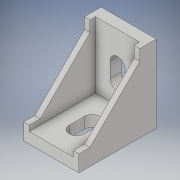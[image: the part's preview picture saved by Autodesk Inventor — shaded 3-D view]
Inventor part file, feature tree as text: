
AUTODESK INVENTOR PART (.ipt)
format: ipt  version: 2019 (Build 230136000, 136)  size: 165,376 bytes
history: native  units: in
note: dims shown in document units (in); Inventor stores cm internally (conversion verified against a paired STEP export)
features: extrude x6, sketch x6
ambient origin geometry x8: Origin, YZ Plane, XZ Plane, XY Plane, X Axis, Y Axis, Z Axis, Center Point
bodies: Solid1 (feature_tree)
feature tree (12):
  extrude  "Extrusion1"  Depth=0.7874in
  extrude  "Extrusion2"  Depth=0.1575in
  extrude  "Extrusion3"  Depth=0.0787in
  extrude  "Extrusion4"  Depth=0.9449in TaperAngle=0.0deg
  extrude  "Extrusion5"  Depth=0.0787in
  extrude  "Extrusion6"  Depth=0.1575in
  sketch  "Sketch1"  dims[d0=1.1024in d1=0.7874in]
  sketch  "Sketch2"  dims[d2=0.1575in d3=0.0in d4=0.1575in]
  sketch  "Sketch3"  dims[d5=0.9449in d6=0.0in d7=0.0787in]
  sketch  "Sketch4"  dims[d8=0.0787in d9=0.9449in d10=0.0in]
  sketch  "Sketch5"  dims[d11=0.0787in d12=0.0787in]
  sketch  "Sketch6"  dims[d13=0.1575in d14=0.1575in d15=0.9449in d16=0.0in d17=0.2165in d18=0.2165in d19=0.9449in d20=0.0in d21=0.2165in d22=0.2165in d23=0.9449in d24=0.0in]
